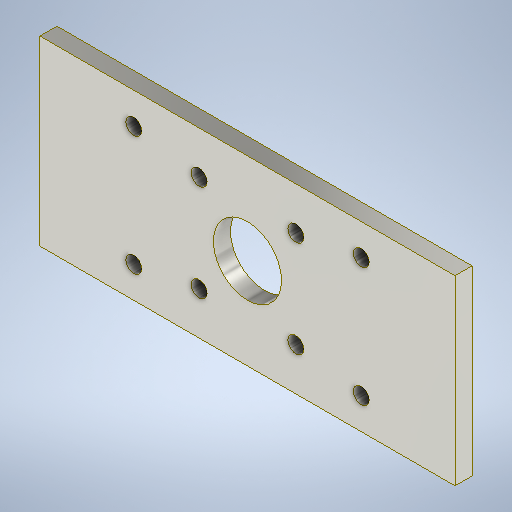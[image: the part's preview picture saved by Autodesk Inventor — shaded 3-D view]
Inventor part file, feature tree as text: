
AUTODESK INVENTOR PART (.ipt)
format: ipt  version: 2025.1 (Build 291241000, 241)  size: 237,568 bytes
history: native  units: mm
features: extrude x2, sketch x2
ambient origin geometry x8: Origin, YZ Plane, XZ Plane, XY Plane, X Axis, Y Axis, Z Axis, Center Point
bodies: Solid1 (feature_tree)
feature tree (4):
  extrude  "Extrusion1"  Depth=48.015mm
  extrude  "Extrusion2"  Depth=10.0mm
  sketch  "Sketch1"  dims[d3=0.0mm d4=48.015mm]
  sketch  "Sketch2"  dims[d5=30.0mm d6=4.007mm d7=4.5mm d8=2.8mm d9=2.8mm d10=6.5mm d11=15.507mm d12=10.0mm d13=0.0mm d14=12.0mm]
